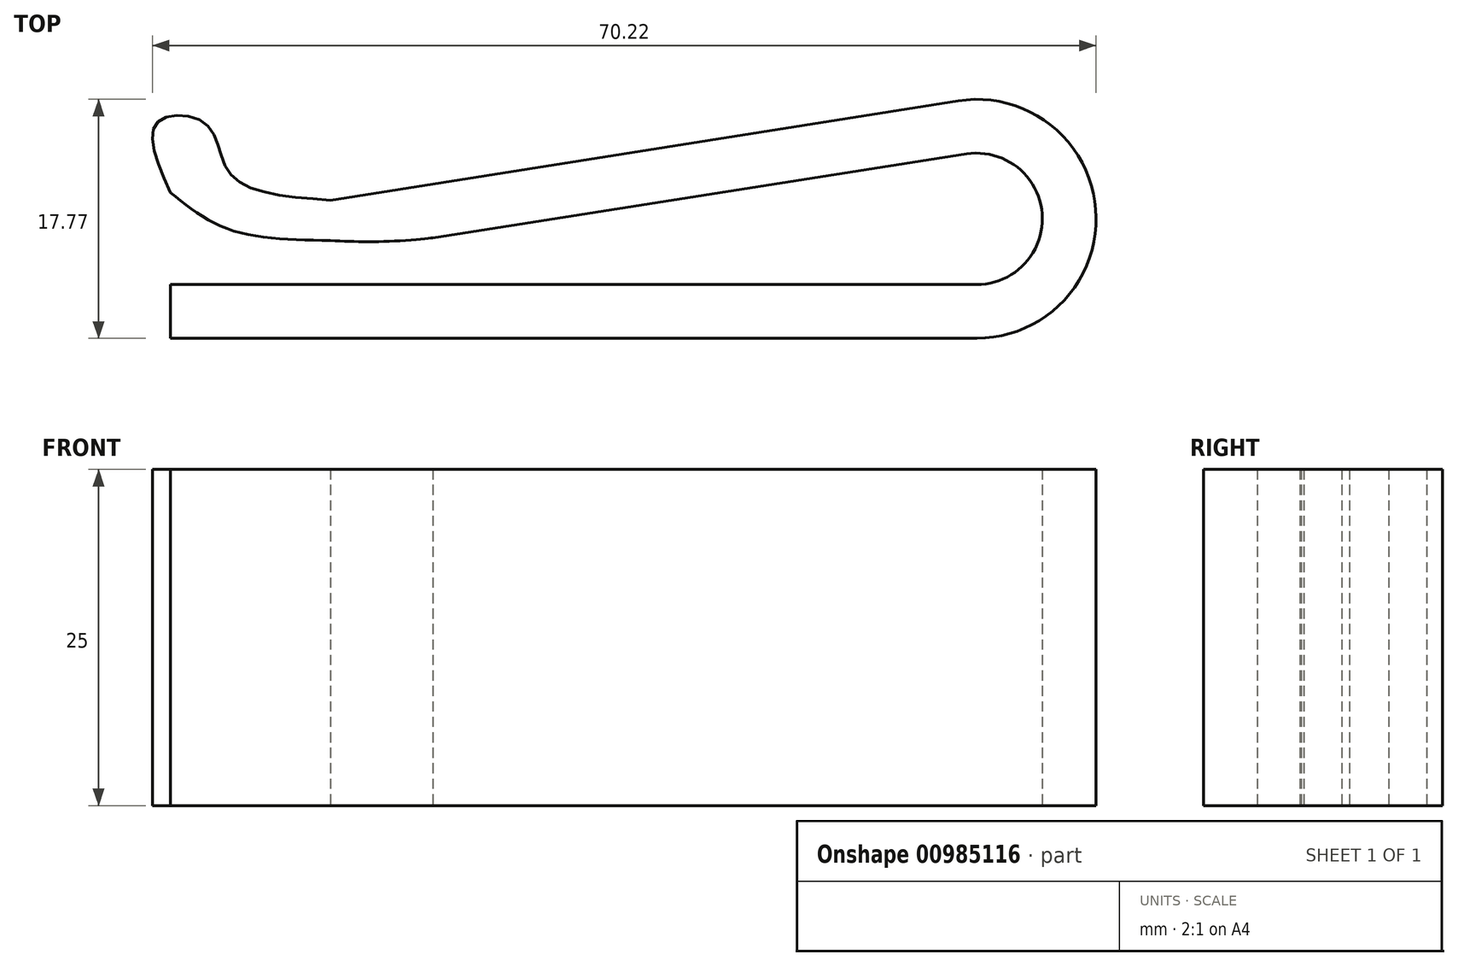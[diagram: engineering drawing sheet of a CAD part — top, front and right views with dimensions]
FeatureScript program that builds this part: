
annotation { "Feature Type Name" : "Feature", "Feature Type Description" : "" }
export const myFeature = defineFeature(function(context is Context, id is Id, definition is map)
    precondition{}
    {
        {
            var Q0;
            Q0=qCreatedBy(makeId("Top.planeOp"),FACE);
            var sketch = newSketch(context, id + "F0", { "sketchPlane" : qUnion([Q0])});
            skLineSegment(sketch, "E0", {"start": v(0, 0) * mm, "end": v(60, 0) * mm});
            skLineSegment(sketch, "E1", {"start": v(60, 0) * mm, "end": v(60, 4.88) * mm});
            skArc(sketch, "E2", {"start": v(60, 0) * mm, "mid": v(64.87, 5.26) * mm, "end": v(59.24, 9.7) * mm});
            skLineSegment(sketch, "E3", {"start": v(19.52, 3.47) * mm, "end": v(59.24, 9.7) * mm});
            skFitSpline(sketch, "E4", {"points": [v(11.91, 3.27) * mm, v(16.55, 3.23) * mm, v(19.52, 3.47) * mm, v(19.52, 3.47) * mm], "startDerivative": vector(7.93, -0.4) * mm, "endDerivative": vector(0.06, 0.01) * mm});
            skLineSegment(sketch, "E5", {"start": v(11.91, 6.27) * mm, "end": v(58.61, 13.66) * mm});
            skLineSegment(sketch, "E6", {"start": v(0, 0) * mm, "end": v(0, -4) * mm});
            skLineSegment(sketch, "E7", {"start": v(0, -4) * mm, "end": v(60, -4) * mm});
            skArc(sketch, "E8.trimOffspring", {"start": v(60, -4) * mm, "mid": v(68.86, 5.58) * mm, "end": v(58.61, 13.66) * mm});
            skPoint(sketch, "E9.2.internal.orphan", {"position": v(1.68, 7.98) * mm});
            skFitSpline(sketch, "E10", {"points": [v(11.91, 6.27) * mm, v(4.47, 8.2) * mm, v(2.65, 11.94) * mm, v(-0.99, 12.04) * mm, v(0, 6.84) * mm], "startDerivative": vector(-30.3, 2.2) * mm, "endDerivative": vector(10.93, -25.08) * mm});
            skPoint(sketch, "E11.0.internal.orphan", {"position": v(16.55, 3) * mm});
            skPoint(sketch, "E11.2.internal.orphan", {"position": v(0, 7.98) * mm});
            skPoint(sketch, "E11.3.internal.orphan", {"position": v(0, 7.98) * mm});
            skFitSpline(sketch, "E12", {"points": [v(11.91, 3.27) * mm, v(4.45, 4.07) * mm, v(0, 6.84) * mm], "startDerivative": vector(-14.76, 0.22) * mm, "endDerivative": vector(-8.88, 7.12) * mm});
            skSolve(sketch);
        }
        {
            var Q0;
            Q0 = qSketchRegion(id + "F0", true);
            extrude(context, id + "F1", {"entities" : qUnion([Q0]), "depth" : 25 * mm, "offsetDistance" : 25.4 * mm});
        }
    });
